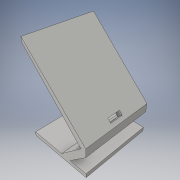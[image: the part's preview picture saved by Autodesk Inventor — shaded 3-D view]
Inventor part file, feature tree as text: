
AUTODESK INVENTOR PART (.ipt)
format: ipt  version: 2016 (Build 200138000, 138)  size: 122,368 bytes
history: native  units: in
note: dims shown in document units (in); Inventor stores cm internally (conversion verified against a paired STEP export)
features: extrude x2, sketch x2
ambient origin geometry x8: Origin, YZ Plane, XZ Plane, XY Plane, X Axis, Y Axis, Z Axis, Center Point
bodies: Solid1 (feature_tree)
feature tree (4):
  extrude  "Extrusion1"  TaperAngle=45.0deg  [1 undecoded]
  extrude  "Extrusion4"  Depth=0.25in
  sketch  "Sketch1"  dims[d0=5.0in d1=45.0deg]
  sketch  "Sketch4"  dims[d2=0.25in d4=1.0in d5=0.5in d6=90.0deg d7=0.25in d8=90.0deg d9=135.0deg d10=0.4in d11=135.0deg d12=4.0in d13=0.0in d22=0.2in d23=90.0deg d24=0.75in d25=0.25in d26=1.0in d27=0.0in]
note: 1 required parameter value undecoded (feature->parameter linkage not recoverable at this tier; creation-order binding heuristic only, values carry confidence <= 0.55)
